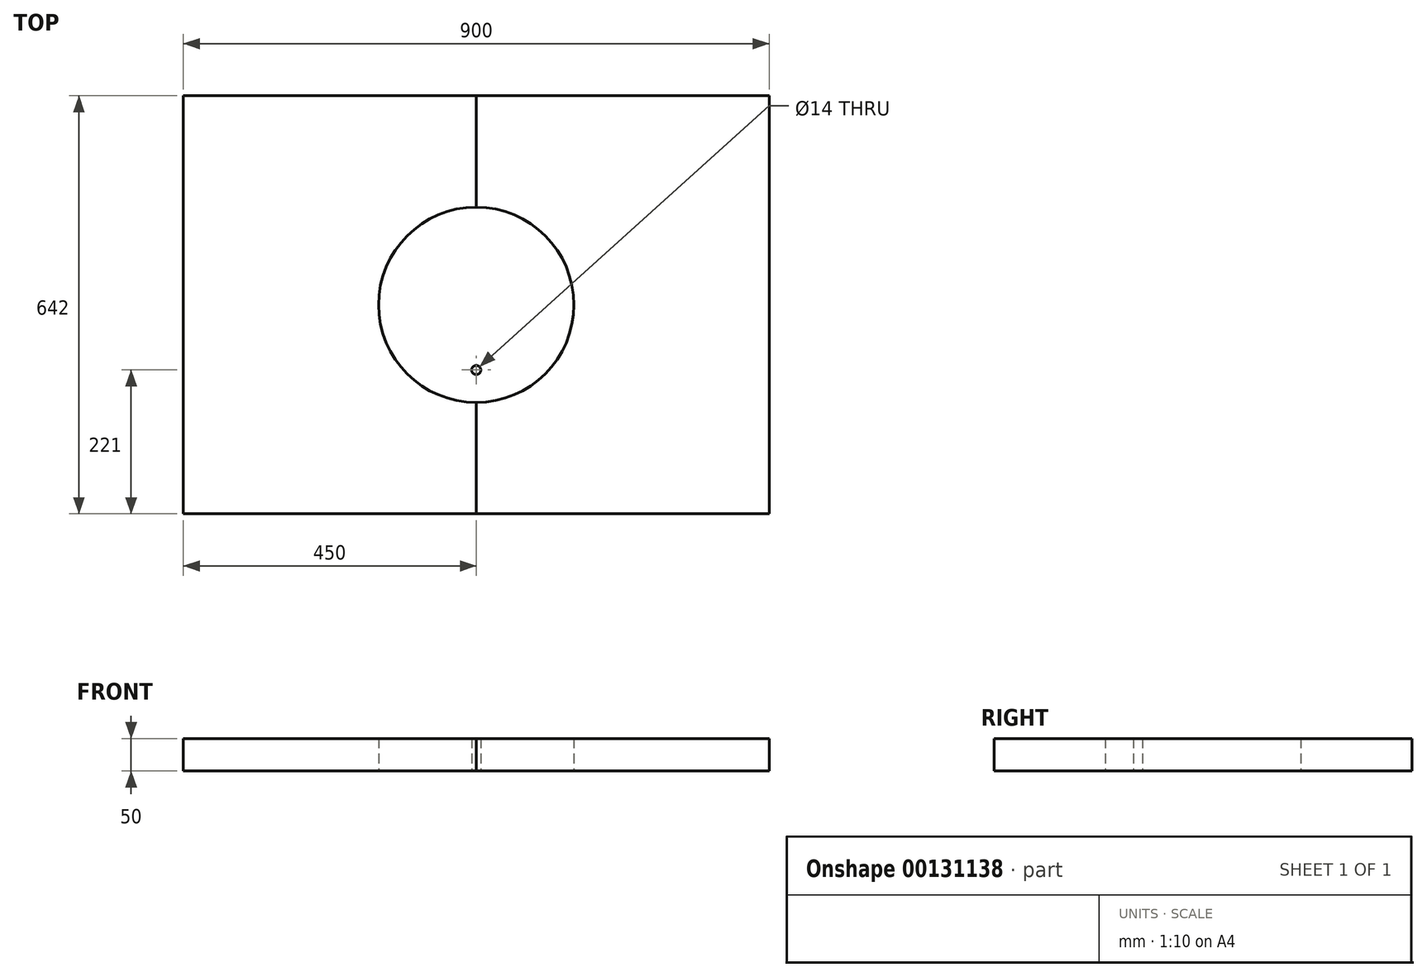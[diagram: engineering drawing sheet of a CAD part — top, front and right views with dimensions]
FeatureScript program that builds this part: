
annotation { "Feature Type Name" : "Feature", "Feature Type Description" : "" }
export const myFeature = defineFeature(function(context is Context, id is Id, definition is map)
    precondition{}
    {
        {
            var Q0;
            Q0=qCreatedBy(makeId("Top.planeOp"),FACE);
            var sketch = newSketch(context, id + "F0", { "sketchPlane" : qUnion([Q0])});
            skLineSegment(sketch, "E0.bottom", {"start": v(450, 321) * mm, "end": v(-450, 321) * mm});
            skLineSegment(sketch, "E0.top", {"start": v(450, -321) * mm, "end": v(-450, -321) * mm});
            skLineSegment(sketch, "E0.left", {"start": v(450, 321) * mm, "end": v(450, -321) * mm});
            skLineSegment(sketch, "E0.right", {"start": v(-450, 321) * mm, "end": v(-450, -321) * mm});
            skPoint(sketch, "E0.middle", {"position": v(0, 0) * mm});
            skCircle(sketch, "E1", {"center": v(0, 0) * mm, "radius": 150 * mm});
            skCircle(sketch, "E2", {"center": v(0, -100) * mm, "radius": 7 * mm});
            skLineSegment(sketch, "E3", {"start": v(0, 321) * mm, "end": v(0, 150) * mm});
            skLineSegment(sketch, "E4", {"start": v(0, -321) * mm, "end": v(0, -150) * mm});
            skSolve(sketch);
        }
        {
            var Q0;
            {var subQ3=sQuery(id+"F0.wireOp",EDGE,"E0.right");Q0=makeQuery(id+"F0.imprint","IMPRINT",FACE,{"disambiguationData":[TD([[makeQuery(id+"F0.imprint","IMPRINT",EDGE,{"derivedFrom":subQ3}),1.0]])]});}
            extrude(context, id + "F1", {"entities" : qUnion([Q0]), "depth" : 50 * mm});
        }
        {
            var Q0;
            {var subQ3=sQuery(id+"F0.wireOp",EDGE,"E0.left");Q0=makeQuery(id+"F0.imprint","IMPRINT",FACE,{"disambiguationData":[TD([[makeQuery(id+"F0.imprint","IMPRINT",EDGE,{"derivedFrom":subQ3}),-1.0]])]});}
            extrude(context, id + "F2", {"entities" : qUnion([Q0]), "depth" : 50 * mm});
        }
        {
            var Q0;
            Q0=makeQuery(id+"F0.imprint","IMPRINT",FACE,{"disambiguationData":[TD([[makeQuery(id+"F0.imprint","IMPRINT",EDGE,{"derivedFrom":sQuery(id+"F0.wireOp",EDGE,"E2")}),-1.0]])]});
            extrude(context, id + "F3", {"entities" : qUnion([Q0]), "depth" : 50 * mm});
        }
    });
